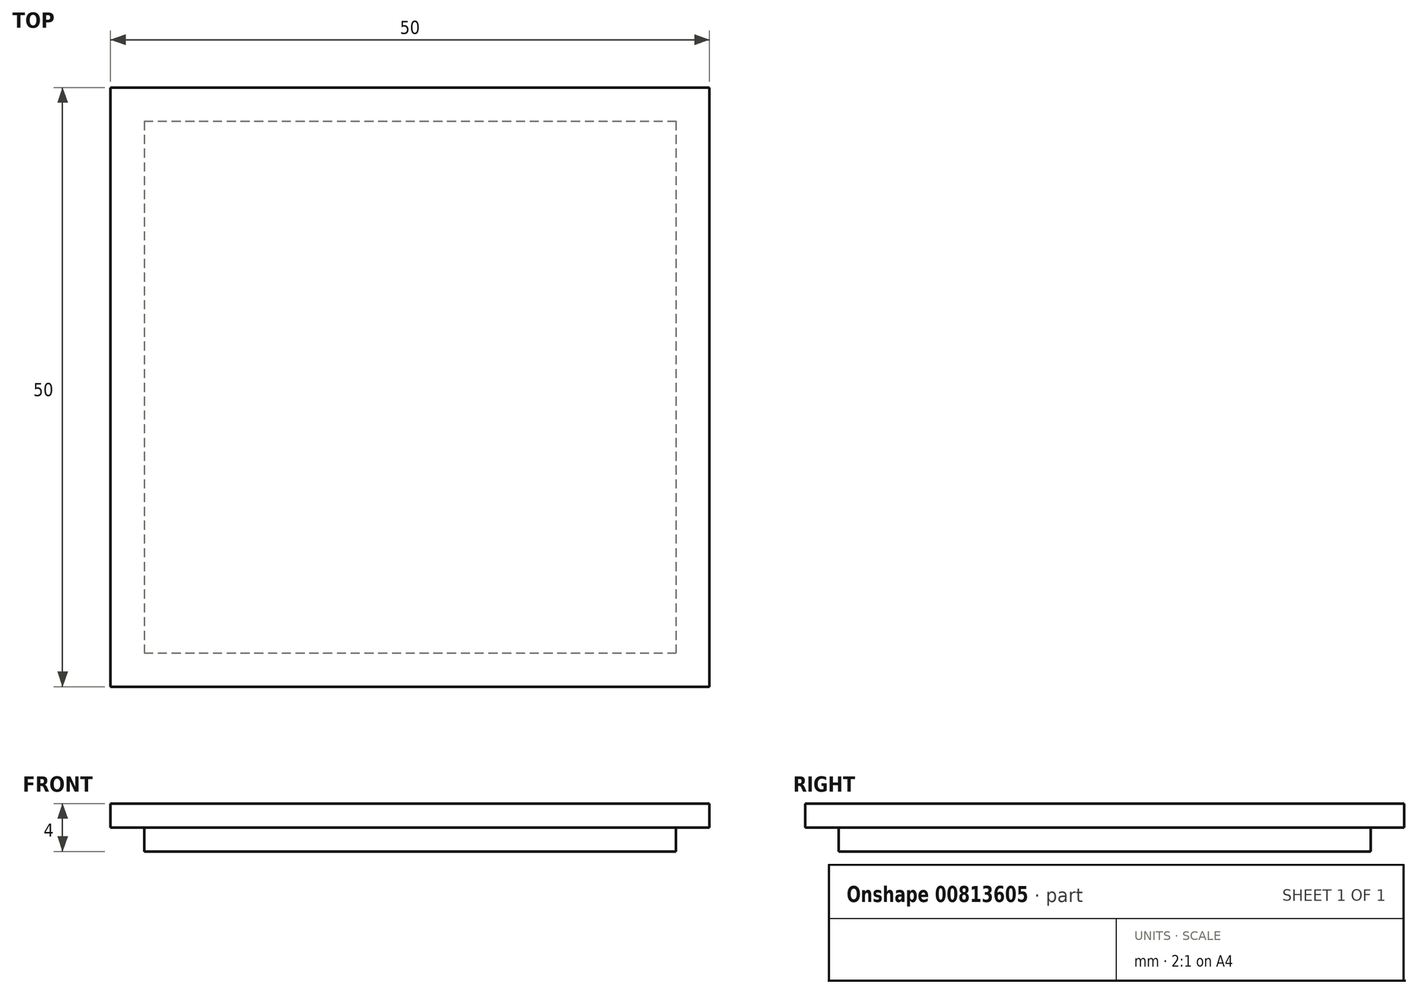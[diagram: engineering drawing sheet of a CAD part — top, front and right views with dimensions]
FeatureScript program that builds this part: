
annotation { "Feature Type Name" : "Feature", "Feature Type Description" : "" }
export const myFeature = defineFeature(function(context is Context, id is Id, definition is map)
    precondition{}
    {
        {
            var Q0;
            Q0=qCreatedBy(makeId("Top.planeOp"),FACE);
            var sketch = newSketch(context, id + "F0", { "sketchPlane" : qUnion([Q0])});
            skLineSegment(sketch, "E0.bottom", {"start": v(-25, 25) * mm, "end": v(25, 25) * mm});
            skLineSegment(sketch, "E0.top", {"start": v(-25, -25) * mm, "end": v(25, -25) * mm});
            skLineSegment(sketch, "E0.left", {"start": v(-25, 25) * mm, "end": v(-25, -25) * mm});
            skLineSegment(sketch, "E0.right", {"start": v(25, 25) * mm, "end": v(25, -25) * mm});
            skPoint(sketch, "E0.middle", {"position": v(0, 0) * mm});
            skLineSegment(sketch, "E1.bottom", {"start": v(-22.2, 22.2) * mm, "end": v(22.2, 22.2) * mm});
            skLineSegment(sketch, "E1.top", {"start": v(-22.2, -22.2) * mm, "end": v(22.2, -22.2) * mm});
            skLineSegment(sketch, "E1.left", {"start": v(-22.2, 22.2) * mm, "end": v(-22.2, -22.2) * mm});
            skLineSegment(sketch, "E1.right", {"start": v(22.2, 22.2) * mm, "end": v(22.2, -22.2) * mm});
            skSolve(sketch);
        }
        {
            var Q0;
            Q0=makeQuery(id+"F0.imprint","IMPRINT",FACE,{"disambiguationData":[TD([[makeQuery(id+"F0.imprint","IMPRINT",EDGE,{"derivedFrom":sQuery(id+"F0.wireOp",EDGE,"E1.bottom")}),-1.0]])]});
            extrude(context, id + "F1", {"entities" : qUnion([Q0]), "oppositeDirection" : true, "depth" : 2 * mm, "offsetDistance" : 25 * mm});
        }
        {
            var Q0;
            Q0=makeQuery(id+"F0.imprint","IMPRINT",FACE,{"disambiguationData":[TD([[makeQuery(id+"F0.imprint","IMPRINT",EDGE,{"derivedFrom":sQuery(id+"F0.wireOp",EDGE,"E1.bottom")}),-1.0]])]});
            var Q1;
            Q1=makeQuery(id+"F0.imprint","IMPRINT",FACE,{"disambiguationData":[TD([[makeQuery(id+"F0.imprint","IMPRINT",EDGE,{"derivedFrom":sQuery(id+"F0.wireOp",EDGE,"E0.bottom")}),-1.0]])]});
            extrude(context, id + "F2", {"entities" : qUnion([Q0, Q1]), "operationType" : NewBodyOperationType.ADD, "depth" : 2 * mm, "offsetDistance" : 25 * mm});
        }
    });
